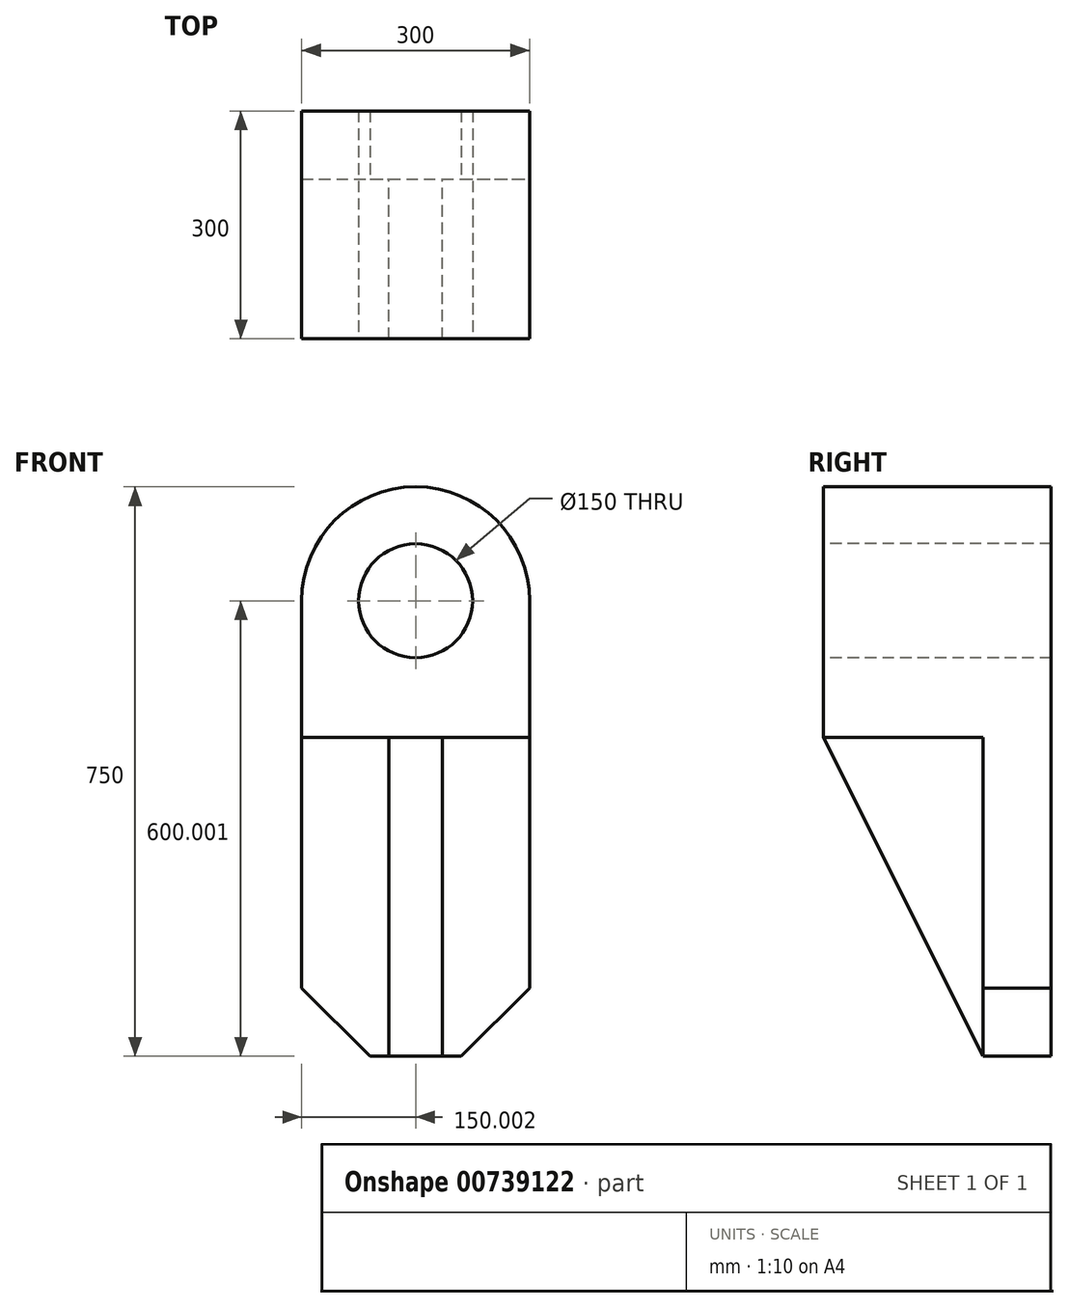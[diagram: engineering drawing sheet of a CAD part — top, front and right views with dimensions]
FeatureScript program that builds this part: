
annotation { "Feature Type Name" : "Feature", "Feature Type Description" : "" }
export const myFeature = defineFeature(function(context is Context, id is Id, definition is map)
    precondition{}
    {
        {
            var Q0;
            Q0=qCreatedBy(makeId("Front.planeOp"),FACE);
            var sketch = newSketch(context, id + "F0", { "sketchPlane" : qUnion([Q0])});
            skLineSegment(sketch, "E0.bottom", {"start": v(-165.19, 289.86) * mm, "end": v(134.81, 289.86) * mm});
            skLineSegment(sketch, "E0.top", {"start": v(-165.19, -310.14) * mm, "end": v(134.81, -310.14) * mm});
            skLineSegment(sketch, "E0.left", {"start": v(-165.19, 289.86) * mm, "end": v(-165.19, -310.14) * mm});
            skLineSegment(sketch, "E0.right", {"start": v(134.81, 289.86) * mm, "end": v(134.81, -310.14) * mm});
            skSolve(sketch);
        }
        {
            var Q0;
            Q0 = qSketchRegion(id + "F0", true);
            extrude(context, id + "F1", {"entities" : qUnion([Q0]), "depth" : 90 * mm, "offsetDistance" : 25 * mm});
        }
        {
            var Q0;
            Q0=makeQuery(id+"F1.opExtrude","CAP_FACE",FACE,{"disambiguationData":[OSD([sQuery(id+"F0.wireOp",EDGE,"E0.bottom"),sQuery(id+"F0.wireOp",EDGE,"E0.top"),sQuery(id+"F0.wireOp",EDGE,"E0.left"),sQuery(id+"F0.wireOp",EDGE,"E0.right")])],"isStart":true});
            var sketch = newSketch(context, id + "F2", { "sketchPlane" : qUnion([Q0])});
            skArc(sketch, "E1", {"start": v(165.19, 289.86) * mm, "mid": v(15.19, 439.86) * mm, "end": v(-134.81, 289.86) * mm});
            skLineSegment(sketch, "E2.0", {"start": v(165.19, 289.86) * mm, "end": v(-134.81, 289.86) * mm});
            skSolve(sketch);
        }
        {
            var Q0;
            Q0 = qSketchRegion(id + "F2", true);
            extrude(context, id + "F3", {"entities" : qUnion([Q0]), "oppositeDirection" : true, "depth" : 300 * mm, "offsetDistance" : 25 * mm});
        }
        {
            var Q0;
            Q0=makeQuery(id+"F1.opExtrude","CAP_FACE",FACE,{"disambiguationData":[OSD([sQuery(id+"F0.wireOp",EDGE,"E0.bottom"),sQuery(id+"F0.wireOp",EDGE,"E0.top"),sQuery(id+"F0.wireOp",EDGE,"E0.left"),sQuery(id+"F0.wireOp",EDGE,"E0.right")])],"isStart":false});
            var sketch = newSketch(context, id + "F4", { "sketchPlane" : qUnion([Q0])});
            skLineSegment(sketch, "E3.bottom", {"start": v(-165.19, 289.86) * mm, "end": v(134.81, 289.86) * mm});
            skLineSegment(sketch, "E3.top", {"start": v(-165.19, 109.86) * mm, "end": v(134.81, 109.86) * mm});
            skLineSegment(sketch, "E3.left", {"start": v(-165.19, 289.86) * mm, "end": v(-165.19, 109.86) * mm});
            skLineSegment(sketch, "E3.right", {"start": v(134.81, 289.86) * mm, "end": v(134.81, 109.86) * mm});
            skSolve(sketch);
        }
        {
            var Q0;
            Q0 = qSketchRegion(id + "F4", true);
            extrude(context, id + "F5", {"entities" : qUnion([Q0]), "depth" : 210 * mm, "offsetDistance" : 25 * mm});
        }
        {
            var Q0;
            Q0=makeQuery(id+"F5.opExtrude","CAP_FACE",FACE,{"disambiguationData":[OSD([sQuery(id+"F4.wireOp",EDGE,"E3.bottom"),sQuery(id+"F4.wireOp",EDGE,"E3.top"),sQuery(id+"F4.wireOp",EDGE,"E3.left"),sQuery(id+"F4.wireOp",EDGE,"E3.right")])],"isStart":false});
            var sketch = newSketch(context, id + "F6", { "sketchPlane" : qUnion([Q0])});
            skCircle(sketch, "E4", {"center": v(-15.19, 289.86) * mm, "radius": 75 * mm});
            skSolve(sketch);
        }
        {
            var Q0;
            Q0 = qSketchRegion(id + "F6", true);
            extrude(context, id + "F7", {"entities" : qUnion([Q0]), "operationType" : NewBodyOperationType.REMOVE, "oppositeDirection" : true, "depth" : 300 * mm, "offsetDistance" : 25 * mm});
        }
        {
            var Q0;
            Q0=makeQuery(id+"F1.opExtrude","SWEPT_BODY",BODY,{"disambiguationData":[OSD([sQuery(id+"F0.wireOp",EDGE,"E0.bottom"),sQuery(id+"F0.wireOp",EDGE,"E0.top"),sQuery(id+"F0.wireOp",EDGE,"E0.left"),sQuery(id+"F0.wireOp",EDGE,"E0.right")])]});
            var Q1;
            Q1=makeQuery(id+"F5.opExtrude","SWEPT_BODY",BODY,{"disambiguationData":[OSD([sQuery(id+"F4.wireOp",EDGE,"E3.bottom"),sQuery(id+"F4.wireOp",EDGE,"E3.top"),sQuery(id+"F4.wireOp",EDGE,"E3.left"),sQuery(id+"F4.wireOp",EDGE,"E3.right")])]});
            var Q2;
            Q2=makeQuery(id+"F3.opExtrude","SWEPT_BODY",BODY,{"disambiguationData":[OSD([sQuery(id+"F2.wireOp",EDGE,"E1"),sQuery(id+"F2.wireOp",EDGE,"E2.0")])]});
            booleanBodies(context, id + "F8", {"operationType" : BooleanOperationType.UNION, "tools" : qUnion([Q0, Q1, Q2])});
        }
        {
            var Q0;
            Q0=makeQuery(id+"F5.opExtrude","SWEPT_FACE",FACE,{"disambiguationData":[OSD([sQuery(id+"F4.wireOp",EDGE,"E3.top")])]});
            var sketch = newSketch(context, id + "F9", { "sketchPlane" : qUnion([Q0])});
            skLineSegment(sketch, "E5.bottom", {"start": v(-50.19, 300) * mm, "end": v(19.81, 300) * mm});
            skLineSegment(sketch, "E5.top", {"start": v(-50.19, 90) * mm, "end": v(19.81, 90) * mm});
            skLineSegment(sketch, "E5.left", {"start": v(-50.19, 300) * mm, "end": v(-50.19, 90) * mm});
            skLineSegment(sketch, "E5.right", {"start": v(19.81, 300) * mm, "end": v(19.81, 90) * mm});
            skPoint(sketch, "E6", {"position": v(-15.19, 300) * mm});
            skSolve(sketch);
        }
        {
            var Q0;
            Q0 = qSketchRegion(id + "F9", true);
            extrude(context, id + "F10", {"entities" : qUnion([Q0]), "operationType" : NewBodyOperationType.ADD, "depth" : 420 * mm, "offsetDistance" : 25 * mm});
        }
        {
            var Q0;
            Q0=makeQuery(id+"F10.opExtrude","SWEPT_FACE",FACE,{"disambiguationData":[OSD([sQuery(id+"F9.wireOp",EDGE,"E5.right")])]});
            var sketch = newSketch(context, id + "F11", { "sketchPlane" : qUnion([Q0])});
            skLineSegment(sketch, "E7", {"start": v(-90, -310.14) * mm, "end": v(-300, 109.86) * mm});
            skLineSegment(sketch, "E8", {"start": v(-300, 109.86) * mm, "end": v(-300, -310.14) * mm});
            skLineSegment(sketch, "E9", {"start": v(-300, -310.14) * mm, "end": v(-90, -310.14) * mm});
            skSolve(sketch);
        }
        {
            var Q0;
            Q0 = qSketchRegion(id + "F11", true);
            extrude(context, id + "F12", {"entities" : qUnion([Q0]), "operationType" : NewBodyOperationType.REMOVE, "oppositeDirection" : true, "depth" : 70 * mm, "offsetDistance" : 25 * mm});
        }
        {
            var Q0;
            {var subQ1=sQuery(id+"F0.wireOp",EDGE,"E0.left");var subQ2=sQuery(id+"F0.wireOp",EDGE,"E0.top");Q0=makeQuery(id+"F10.boolean.opBoolean","SPLIT",FACE,{"disambiguationData":[TD([makeQuery(id+"F1.opExtrude","SWEPT_FACE",FACE,{"disambiguationData":[OSD([subQ1])]})])],"derivedFrom":makeQuery(id+"F1.opExtrude","CAP_FACE",FACE,{"disambiguationData":[OSD([sQuery(id+"F0.wireOp",EDGE,"E0.bottom"),subQ2,subQ1,sQuery(id+"F0.wireOp",EDGE,"E0.right")])],"isStart":false})});}
            var sketch = newSketch(context, id + "F13", { "sketchPlane" : qUnion([Q0])});
            skLineSegment(sketch, "E10", {"start": v(-165.19, -310.14) * mm, "end": v(-165.19, -220.14) * mm, "construction": true});
            skLineSegment(sketch, "E11", {"start": v(-165.19, -310.14) * mm, "end": v(-75.19, -310.14) * mm, "construction": true});
            skLineSegment(sketch, "E12", {"start": v(-165.19, -220.14) * mm, "end": v(-75.19, -310.14) * mm});
            skLineSegment(sketch, "E13", {"start": v(-165.19, -220.14) * mm, "end": v(-165.19, -310.14) * mm});
            skLineSegment(sketch, "E14", {"start": v(-75.19, -310.14) * mm, "end": v(-165.19, -310.14) * mm});
            skSolve(sketch);
        }
        {
            var Q0;
            Q0 = qSketchRegion(id + "F13", true);
            extrude(context, id + "F14", {"entities" : qUnion([Q0]), "operationType" : NewBodyOperationType.REMOVE, "oppositeDirection" : true, "depth" : 90 * mm, "offsetDistance" : 25 * mm});
        }
        {
            var Q0;
            {var subQ0=sQuery(id+"F0.wireOp",EDGE,"E0.right");var subQ1=sQuery(id+"F0.wireOp",EDGE,"E0.top");Q0=makeQuery(id+"F10.boolean.opBoolean","SPLIT",FACE,{"disambiguationData":[TD([makeQuery(id+"F1.opExtrude","SWEPT_FACE",FACE,{"disambiguationData":[OSD([subQ0])]})])],"derivedFrom":makeQuery(id+"F1.opExtrude","CAP_FACE",FACE,{"disambiguationData":[OSD([sQuery(id+"F0.wireOp",EDGE,"E0.bottom"),subQ1,sQuery(id+"F0.wireOp",EDGE,"E0.left"),subQ0])],"isStart":false})});}
            var sketch = newSketch(context, id + "F15", { "sketchPlane" : qUnion([Q0])});
            skLineSegment(sketch, "E15", {"start": v(134.81, -310.14) * mm, "end": v(44.81, -310.14) * mm});
            skLineSegment(sketch, "E16", {"start": v(134.81, -310.14) * mm, "end": v(134.81, -220.14) * mm});
            skLineSegment(sketch, "E17", {"start": v(44.81, -310.14) * mm, "end": v(134.81, -220.14) * mm});
            skSolve(sketch);
        }
        {
            var Q0;
            Q0 = qSketchRegion(id + "F15", true);
            extrude(context, id + "F16", {"entities" : qUnion([Q0]), "operationType" : NewBodyOperationType.REMOVE, "oppositeDirection" : true, "depth" : 90 * mm, "offsetDistance" : 25 * mm});
        }
    });
